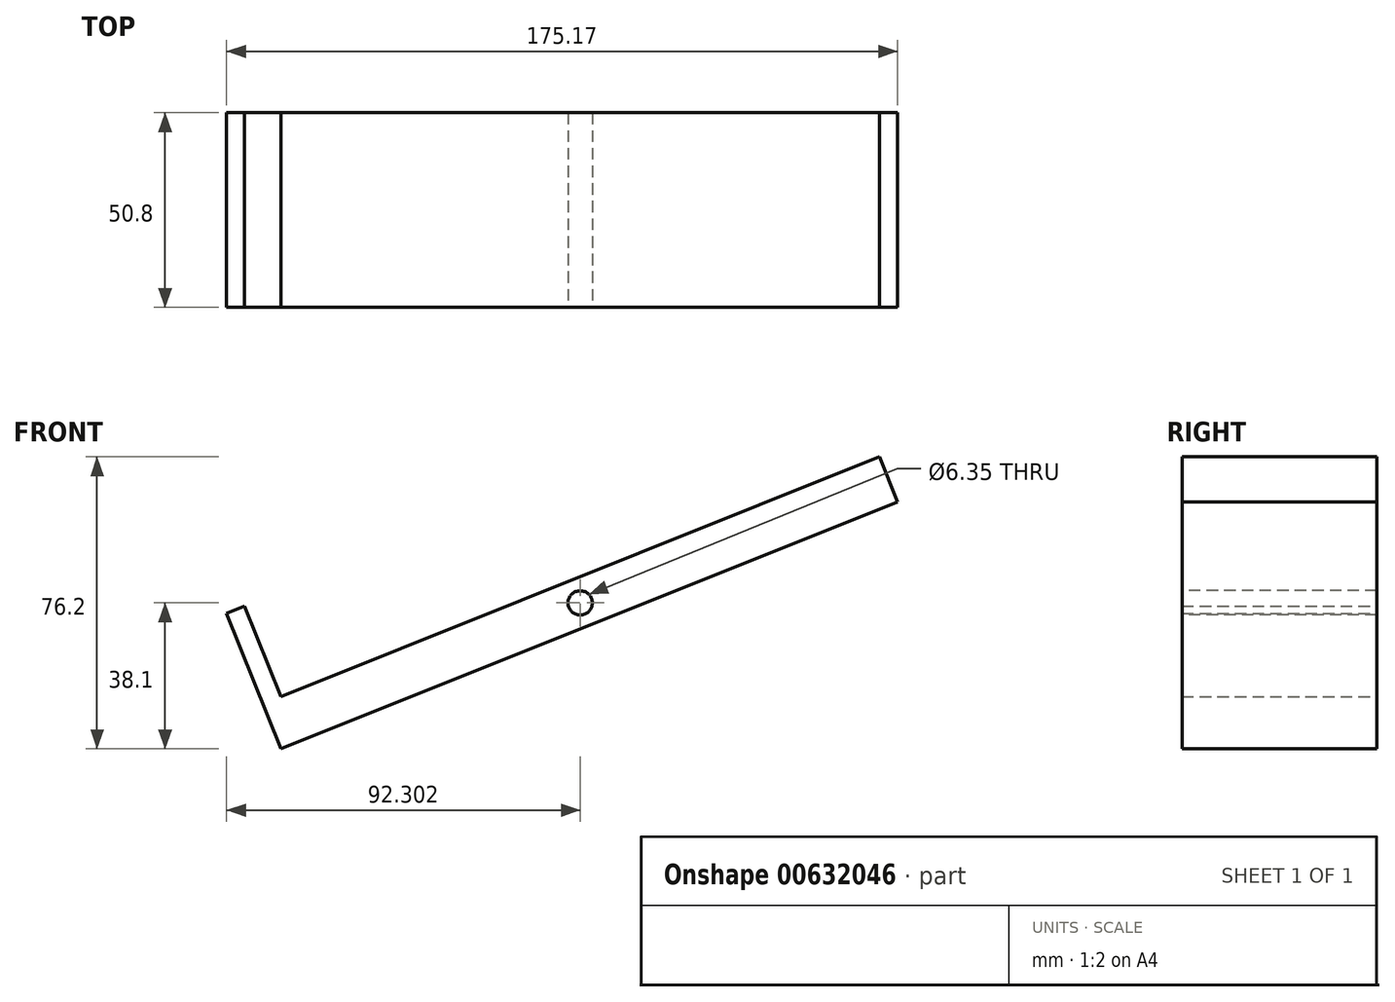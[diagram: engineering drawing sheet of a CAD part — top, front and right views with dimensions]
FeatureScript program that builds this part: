
annotation { "Feature Type Name" : "Feature", "Feature Type Description" : "" }
export const myFeature = defineFeature(function(context is Context, id is Id, definition is map)
    precondition{}
    {
        {
            var Q0;
            Q0=qCreatedBy(makeId("Front.planeOp"),FACE);
            var sketch = newSketch(context, id + "F0", { "sketchPlane" : qUnion([Q0])});
            skLineSegment(sketch, "E0", {"start": v(0, 0) * mm, "end": v(-14.15, 35.37) * mm});
            skLineSegment(sketch, "E1", {"start": v(-14.15, 35.37) * mm, "end": v(-9.43, 37.26) * mm});
            skLineSegment(sketch, "E2", {"start": v(-9.43, 37.26) * mm, "end": v(0, 13.68) * mm});
            skLineSegment(sketch, "E3", {"start": v(0, 13.68) * mm, "end": v(156.3, 76.2) * mm});
            skLineSegment(sketch, "E4", {"start": v(156.3, 76.2) * mm, "end": v(161.02, 64.4) * mm});
            skLineSegment(sketch, "E5", {"start": v(161.02, 64.4) * mm, "end": v(0, 0) * mm});
            skLineSegment(sketch, "E6", {"start": v(80.51, 32.2) * mm, "end": v(56.38, 0) * mm});
            skLineSegment(sketch, "E7", {"start": v(56.38, 0) * mm, "end": v(61.46, 0) * mm});
            skLineSegment(sketch, "E8", {"start": v(61.46, 0) * mm, "end": v(80.51, 25.42) * mm});
            skLineSegment(sketch, "E9", {"start": v(80.51, 25.42) * mm, "end": v(99.56, 0) * mm});
            skLineSegment(sketch, "E10", {"start": v(99.56, 0) * mm, "end": v(104.64, 0) * mm});
            skLineSegment(sketch, "E11", {"start": v(104.64, 0) * mm, "end": v(80.51, 32.2) * mm});
            skSolve(sketch);
        }
        {
            var Q0;
            Q0 = qSketchRegion(id + "F0", true);
            extrude(context, id + "F1", {"entities" : qUnion([Q0]), "depth" : 50.8 * mm, "offsetDistance" : 25.4 * mm});
        }
        {
            var Q0;
            Q0=makeQuery(id+"F1.opExtrude","CAP_FACE",FACE,{"disambiguationData":[OSD([sQuery(id+"F0.wireOp",EDGE,"E6"),sQuery(id+"F0.wireOp",EDGE,"E7"),sQuery(id+"F0.wireOp",EDGE,"E8"),sQuery(id+"F0.wireOp",EDGE,"E9"),sQuery(id+"F0.wireOp",EDGE,"E10"),sQuery(id+"F0.wireOp",EDGE,"E11")])],"isStart":false});
            var sketch = newSketch(context, id + "F2", { "sketchPlane" : qUnion([Q0])});
            skLineSegment(sketch, "E12", {"start": v(80.51, 32.2) * mm, "end": v(117.38, 0) * mm});
            skLineSegment(sketch, "E13", {"start": v(117.38, 0) * mm, "end": v(41.98, -5.04) * mm});
            skLineSegment(sketch, "E14", {"start": v(41.98, -5.04) * mm, "end": v(80.51, 32.2) * mm});
            skSolve(sketch);
        }
        {
            var Q0;
            Q0 = qSketchRegion(id + "F2", true);
            extrude(context, id + "F3", {"entities" : qUnion([Q0]), "operationType" : NewBodyOperationType.REMOVE, "oppositeDirection" : true, "depth" : 50.8 * mm, "offsetDistance" : 25.4 * mm});
        }
        {
            var Q0;
            Q0=makeQuery(id+"F1.opExtrude","CAP_FACE",FACE,{"disambiguationData":[OSD([sQuery(id+"F0.wireOp",EDGE,"E0"),sQuery(id+"F0.wireOp",EDGE,"E1"),sQuery(id+"F0.wireOp",EDGE,"E2"),sQuery(id+"F0.wireOp",EDGE,"E3"),sQuery(id+"F0.wireOp",EDGE,"E4"),sQuery(id+"F0.wireOp",EDGE,"E5")])],"isStart":false});
            var sketch = newSketch(context, id + "F4", { "sketchPlane" : qUnion([Q0])});
            skCircle(sketch, "E15", {"center": v(78.15, 38.1) * mm, "radius": 3.17 * mm});
            skPoint(sketch, "E16", {"position": v(78.15, 44.94) * mm});
            skSolve(sketch);
        }
        {
            var Q0;
            Q0 = qSketchRegion(id + "F4", true);
            extrude(context, id + "F5", {"entities" : qUnion([Q0]), "operationType" : NewBodyOperationType.REMOVE, "oppositeDirection" : true, "depth" : 50.8 * mm, "offsetDistance" : 25.4 * mm});
        }
    });
